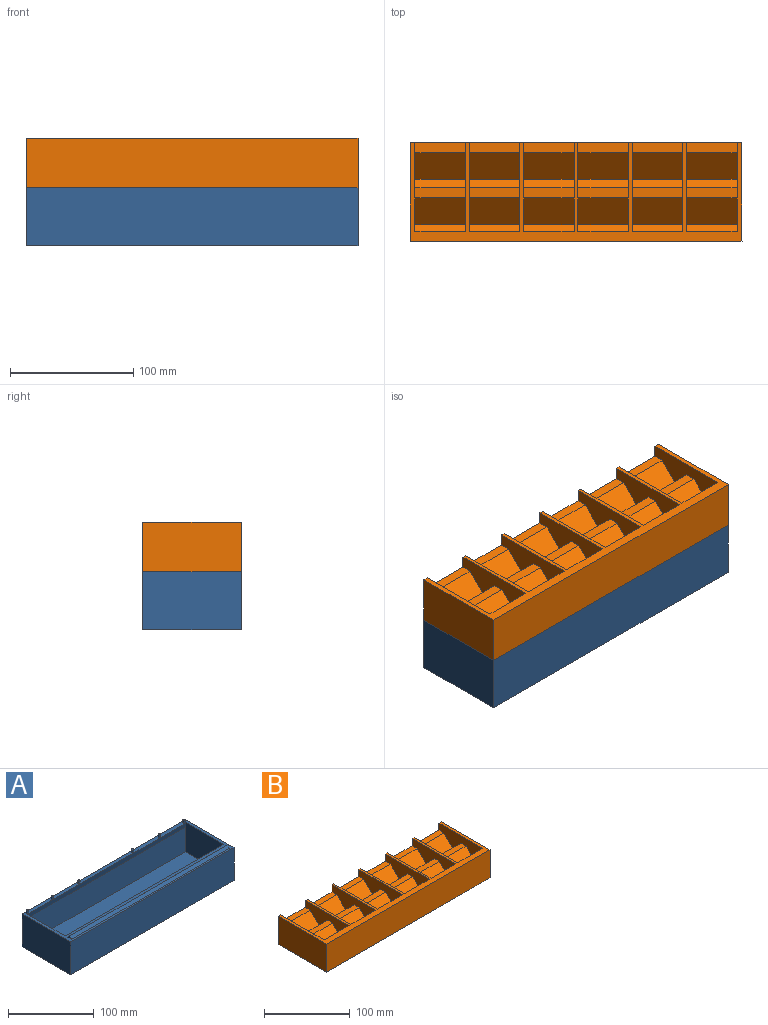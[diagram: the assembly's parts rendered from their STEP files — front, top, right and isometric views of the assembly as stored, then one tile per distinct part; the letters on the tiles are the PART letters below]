
ASSEMBLY  parts=2 mates=1
PART A: 28 faces, bbox 269x80x51 mm
  f0: plane 261x35.19mm, normal (0,-1,0), area 9183.4mm2, adj f1,f2,f4,f15
  f1: plane 63x42mm, normal (1,0,0), area 2641.8mm2, adj f0,f3,f4,f5,f15
  f2: plane 63x42mm, normal (-1,0,0), area 2641.8mm2, adj f0,f3,f4,f5,f15
  f3: plane 261x42mm, normal (0,1,0), area 10962mm2, adj f1,f2,f4,f5
  f4: plane 261x63mm, normal (0,0,1), area 16443mm2, adj f0,f1,f2,f3
  f5: plane 269x80mm, normal (0,0,1), area 3697.2mm2, adj f1,f2,f3,f7,f8,f9,f10,f11
  f6: plane 269x80mm, normal (0,0,-1), area 21520mm2, adj f7,f8,f9,f10
  f7: plane 269x47mm, normal (0,1,0), area 12643mm2, adj f5,f6,f9,f10
  f8: plane 269x47mm, normal (0,-1,0), area 12643mm2, adj f5,f6,f9,f10
  f9: plane 80x47mm, normal (1,0,0), area 3760mm2, adj f5,f6,f7,f8
  f10: plane 80x47mm, normal (-1,0,0), area 3760mm2, adj f5,f6,f7,f8
  f11: plane 260x3.21mm, normal (0,0.71,0.71), area 1179.8mm2, adj f5,f12,f13,f14
  f12: plane 260x3.21mm, normal (0,-0.71,0.71), area 1179.8mm2, adj f5,f11,f13,f14
  f13: plane 6.42x3.21mm, normal (1,0,0), area 10.3mm2, adj f5,f11,f12
  f14: plane 6.42x3.21mm, normal (-1,0,0), area 10.3mm2, adj f5,f11,f12
  f15: plane 261x6.81mm, normal (0,-0.98,-0.18), area 1807.9mm2, adj f0,f1,f2,f5
  f16: cylinder r=1.38mm len=4mm, axis (0,0,-1), area 34.6mm2, adj f5,f17
  f17: plane 2.75x2.75mm, normal (0,0,1), area 5.9mm2, adj f16
  f18: cylinder r=1.38mm len=4mm, axis (0,0,-1), area 34.6mm2, adj f5,f19
  f19: plane 2.75x2.75mm, normal (0,0,1), area 5.9mm2, adj f18
  f20: cylinder r=1.38mm len=4mm, axis (0,0,-1), area 34.6mm2, adj f5,f21
  f21: plane 2.75x2.75mm, normal (0,0,1), area 5.9mm2, adj f20
  f22: cylinder r=1.38mm len=4mm, axis (0,0,-1), area 34.6mm2, adj f5,f23
  f23: plane 2.75x2.75mm, normal (0,0,1), area 5.9mm2, adj f22
  f24: cylinder r=1.38mm len=4mm, axis (0,0,-1), area 34.6mm2, adj f5,f25
  f25: plane 2.75x2.75mm, normal (0,0,1), area 5.9mm2, adj f24
  f26: cylinder r=1.38mm len=4mm, axis (0,0,-1), area 34.6mm2, adj f5,f27
  f27: plane 2.75x2.75mm, normal (0,0,1), area 5.9mm2, adj f26
PART B: 136 faces, bbox 269x80x40 mm
  f0: plane 269x80mm, normal (0,0,-1), area 4885.6mm2, adj f2,f5,f15,f18,f28,f31,f41,f44
  f1: plane 41x12.27mm, normal (0,0.95,-0.31), area 529mm2, adj f12,f13,f88,f114
  f2: plane 41x19.14mm, normal (0,0.71,-0.71), area 1109.6mm2, adj f0,f3,f92,f119
  f3: plane 41x19.14mm, normal (0,-0.71,-0.71), area 1109.6mm2, adj f2,f4,f92,f119
  f4: plane 41x22.37mm, normal (0,0.71,-0.71), area 1296.8mm2, adj f3,f5,f90,f117
  f5: plane 41x22.37mm, normal (0,-1,0), area 917mm2, adj f0,f4,f90,f117
  f6: plane 41x8.1mm, normal (0,0,1), area 332.2mm2, adj f7,f80,f88,f114
  f7: plane 41x21.73mm, normal (0,-0.71,0.71), area 1259.8mm2, adj f6,f8,f88,f114
  f8: plane 41x10.16mm, normal (0,0.71,0.71), area 588.9mm2, adj f7,f9,f88,f114
  f9: plane 41x11.57mm, normal (0,0.96,-0.28), area 494.8mm2, adj f8,f10,f88,f114
  f10: plane 41x8.1mm, normal (0,0,1), area 332.2mm2, adj f9,f11,f88,f114
  f11: plane 41x21.74mm, normal (0,-0.71,0.71), area 1260.8mm2, adj f10,f12,f88,f114
  f12: plane 41x9.47mm, normal (0,0.71,0.71), area 549.2mm2, adj f1,f11,f88,f114
  f13: plane 41x10mm, normal (0,1,0), area 410mm2, adj f1,f83,f88,f114
  f14: plane 41x12.27mm, normal (0,0.95,-0.31), area 529mm2, adj f25,f26,f108,f115
  f15: plane 41x19.14mm, normal (0,0.71,-0.71), area 1109.6mm2, adj f0,f16,f113,f118
  f16: plane 41x19.14mm, normal (0,-0.71,-0.71), area 1109.6mm2, adj f15,f17,f113,f118
  f17: plane 41x22.37mm, normal (0,0.71,-0.71), area 1296.8mm2, adj f16,f18,f111,f116
  f18: plane 41x22.37mm, normal (0,-1,0), area 917mm2, adj f0,f17,f111,f116
  f19: plane 41x8.1mm, normal (0,0,1), area 332.2mm2, adj f20,f80,f108,f115
  f20: plane 41x21.73mm, normal (0,-0.71,0.71), area 1259.8mm2, adj f19,f21,f108,f115
  f21: plane 41x10.16mm, normal (0,0.71,0.71), area 588.9mm2, adj f20,f22,f108,f115
  f22: plane 41x11.57mm, normal (0,0.96,-0.28), area 494.8mm2, adj f21,f23,f108,f115
  f23: plane 41x8.1mm, normal (0,0,1), area 332.2mm2, adj f22,f24,f108,f115
  f24: plane 41x21.74mm, normal (0,-0.71,0.71), area 1260.8mm2, adj f23,f25,f108,f115
  f25: plane 41x9.47mm, normal (0,0.71,0.71), area 549.2mm2, adj f14,f24,f108,f115
  f26: plane 41x10mm, normal (0,1,0), area 410mm2, adj f14,f83,f108,f115
  f27: plane 41x12.27mm, normal (0,0.95,-0.31), area 529mm2, adj f38,f39,f105,f109
  f28: plane 41x19.14mm, normal (0,0.71,-0.71), area 1109.6mm2, adj f0,f29,f107,f112
  f29: plane 41x19.14mm, normal (0,-0.71,-0.71), area 1109.6mm2, adj f28,f30,f107,f112
  f30: plane 41x22.37mm, normal (0,0.71,-0.71), area 1296.8mm2, adj f29,f31,f106,f110
  f31: plane 41x22.37mm, normal (0,-1,0), area 917mm2, adj f0,f30,f106,f110
  f32: plane 41x8.1mm, normal (0,0,1), area 332.2mm2, adj f33,f80,f105,f109
  f33: plane 41x21.73mm, normal (0,-0.71,0.71), area 1259.8mm2, adj f32,f34,f105,f109
  f34: plane 41x10.16mm, normal (0,0.71,0.71), area 588.9mm2, adj f33,f35,f105,f109
  f35: plane 41x11.57mm, normal (0,0.96,-0.28), area 494.8mm2, adj f34,f36,f105,f109
  f36: plane 41x8.1mm, normal (0,0,1), area 332.2mm2, adj f35,f37,f105,f109
  f37: plane 41x21.74mm, normal (0,-0.71,0.71), area 1260.8mm2, adj f36,f38,f105,f109
  f38: plane 41x9.47mm, normal (0,0.71,0.71), area 549.2mm2, adj f27,f37,f105,f109
  f39: plane 41x10mm, normal (0,1,0), area 410mm2, adj f27,f83,f105,f109
  f40: plane 41x12.27mm, normal (0,0.95,-0.31), area 529mm2, adj f51,f52,f84,f99
  f41: plane 41x19.14mm, normal (0,0.71,-0.71), area 1109.6mm2, adj f0,f42,f86,f104
  f42: plane 41x19.14mm, normal (0,-0.71,-0.71), area 1109.6mm2, adj f41,f43,f86,f104
  f43: plane 41x22.37mm, normal (0,0.71,-0.71), area 1296.8mm2, adj f42,f44,f85,f102
  f44: plane 41x22.37mm, normal (0,-1,0), area 917mm2, adj f0,f43,f85,f102
  f45: plane 41x8.1mm, normal (0,0,1), area 332.2mm2, adj f46,f80,f84,f99
  f46: plane 41x21.73mm, normal (0,-0.71,0.71), area 1259.8mm2, adj f45,f47,f84,f99
  f47: plane 41x10.16mm, normal (0,0.71,0.71), area 588.9mm2, adj f46,f48,f84,f99
  f48: plane 41x11.57mm, normal (0,0.96,-0.28), area 494.8mm2, adj f47,f49,f84,f99
  f49: plane 41x8.1mm, normal (0,0,1), area 332.2mm2, adj f48,f50,f84,f99
  f50: plane 41x21.74mm, normal (0,-0.71,0.71), area 1260.8mm2, adj f49,f51,f84,f99
  f51: plane 41x9.47mm, normal (0,0.71,0.71), area 549.2mm2, adj f40,f50,f84,f99
  f52: plane 41x10mm, normal (0,1,0), area 410mm2, adj f40,f83,f84,f99
  f53: plane 41x12.27mm, normal (0,0.95,-0.31), area 529mm2, adj f64,f65,f93,f100
  f54: plane 41x19.14mm, normal (0,0.71,-0.71), area 1109.6mm2, adj f0,f55,f98,f103
  f55: plane 41x19.14mm, normal (0,-0.71,-0.71), area 1109.6mm2, adj f54,f56,f98,f103
  f56: plane 41x22.37mm, normal (0,0.71,-0.71), area 1296.8mm2, adj f55,f57,f96,f101
  f57: plane 41x22.37mm, normal (0,-1,0), area 917mm2, adj f0,f56,f96,f101
  f58: plane 41x8.1mm, normal (0,0,1), area 332.2mm2, adj f59,f80,f93,f100
  f59: plane 41x21.73mm, normal (0,-0.71,0.71), area 1259.8mm2, adj f58,f60,f93,f100
  f60: plane 41x10.16mm, normal (0,0.71,0.71), area 588.9mm2, adj f59,f61,f93,f100
  f61: plane 41x11.57mm, normal (0,0.96,-0.28), area 494.8mm2, adj f60,f62,f93,f100
  f62: plane 41x8.1mm, normal (0,0,1), area 332.2mm2, adj f61,f63,f93,f100
  f63: plane 41x21.74mm, normal (0,-0.71,0.71), area 1260.8mm2, adj f62,f64,f93,f100
  f64: plane 41x9.47mm, normal (0,0.71,0.71), area 549.2mm2, adj f53,f63,f93,f100
  f65: plane 41x10mm, normal (0,1,0), area 410mm2, adj f53,f83,f93,f100
  f66: plane 41x12.27mm, normal (0,0.95,-0.31), area 529mm2, adj f77,f78,f87,f94
  f67: plane 41x19.14mm, normal (0,0.71,-0.71), area 1109.6mm2, adj f0,f68,f91,f97
  f68: plane 41x19.14mm, normal (0,-0.71,-0.71), area 1109.6mm2, adj f67,f69,f91,f97
  f69: plane 41x22.37mm, normal (0,0.71,-0.71), area 1296.8mm2, adj f68,f70,f89,f95
  f70: plane 41x22.37mm, normal (0,-1,0), area 917mm2, adj f0,f69,f89,f95
  f71: plane 41x8.1mm, normal (0,0,1), area 332.2mm2, adj f72,f80,f87,f94
  f72: plane 41x21.73mm, normal (0,-0.71,0.71), area 1259.8mm2, adj f71,f73,f87,f94
  f73: plane 41x10.16mm, normal (0,0.71,0.71), area 588.9mm2, adj f72,f74,f87,f94
  f74: plane 41x11.57mm, normal (0,0.96,-0.28), area 494.8mm2, adj f73,f75,f87,f94
  f75: plane 41x8.1mm, normal (0,0,1), area 332.2mm2, adj f74,f76,f87,f94
  f76: plane 41x21.74mm, normal (0,-0.71,0.71), area 1260.8mm2, adj f75,f77,f87,f94
  f77: plane 41x9.47mm, normal (0,0.71,0.71), area 549.2mm2, adj f66,f76,f87,f94
  f78: plane 41x10mm, normal (0,1,0), area 410mm2, adj f66,f83,f87,f94
  f79: plane 269x40mm, normal (0,-1,0), area 10760mm2, adj f0,f81,f82,f83
  f80: plane 269x40mm, normal (0,1,0), area 8300mm2, adj f0,f6,f19,f32,f45,f58,f71,f81
  f81: plane 80x40mm, normal (1,0,0), area 3200mm2, adj f0,f79,f80,f83
  f82: plane 80x40mm, normal (-1,0,0), area 3200mm2, adj f0,f79,f80,f83
  f83: plane 269x80mm, normal (0,0,1), area 3832.9mm2, adj f13,f26,f39,f52,f65,f78,f79,f80
  f84: plane 75.88x31.74mm, normal (1,0,0), area 1477.4mm2, adj f40,f45,f46,f47,f48,f49,f50,f51
  f85: plane 22.37x22.37mm, normal (1,0,0), area 250.1mm2, adj f0,f43,f44
  f86: plane 38.27x19.14mm, normal (1,0,0), area 366.2mm2, adj f0,f41,f42
  f87: plane 75.88x31.74mm, normal (-1,0,0), area 1477.4mm2, adj f66,f71,f72,f73,f74,f75,f76,f77
  f88: plane 75.88x31.74mm, normal (1,0,0), area 1477.4mm2, adj f1,f6,f7,f8,f9,f10,f11,f12
  f89: plane 22.37x22.37mm, normal (-1,0,0), area 250.1mm2, adj f0,f69,f70
  f90: plane 22.37x22.37mm, normal (1,0,0), area 250.1mm2, adj f0,f4,f5
  f91: plane 38.27x19.14mm, normal (-1,0,0), area 366.2mm2, adj f0,f67,f68
  f92: plane 38.27x19.14mm, normal (1,0,0), area 366.2mm2, adj f0,f2,f3
  f93: plane 75.88x31.74mm, normal (-1,0,0), area 1477.4mm2, adj f53,f58,f59,f60,f61,f62,f63,f64
  f94: plane 75.88x31.74mm, normal (1,0,0), area 1477.4mm2, adj f66,f71,f72,f73,f74,f75,f76,f77
  f95: plane 22.37x22.37mm, normal (1,0,0), area 250.1mm2, adj f0,f69,f70
  f96: plane 22.37x22.37mm, normal (-1,0,0), area 250.1mm2, adj f0,f56,f57
  f97: plane 38.27x19.14mm, normal (1,0,0), area 366.2mm2, adj f0,f67,f68
  f98: plane 38.27x19.14mm, normal (-1,0,0), area 366.2mm2, adj f0,f54,f55
  f99: plane 75.88x31.74mm, normal (-1,0,0), area 1477.4mm2, adj f40,f45,f46,f47,f48,f49,f50,f51
  f100: plane 75.88x31.74mm, normal (1,0,0), area 1477.4mm2, adj f53,f58,f59,f60,f61,f62,f63,f64
  f101: plane 22.37x22.37mm, normal (1,0,0), area 250.1mm2, adj f0,f56,f57
  f102: plane 22.37x22.37mm, normal (-1,0,0), area 250.1mm2, adj f0,f43,f44
  f103: plane 38.27x19.14mm, normal (1,0,0), area 366.2mm2, adj f0,f54,f55
  f104: plane 38.27x19.14mm, normal (-1,0,0), area 366.2mm2, adj f0,f41,f42
  f105: plane 75.88x31.74mm, normal (-1,0,0), area 1477.4mm2, adj f27,f32,f33,f34,f35,f36,f37,f38
  f106: plane 22.37x22.37mm, normal (-1,0,0), area 250.1mm2, adj f0,f30,f31
  f107: plane 38.27x19.14mm, normal (-1,0,0), area 366.2mm2, adj f0,f28,f29
  f108: plane 75.88x31.74mm, normal (-1,0,0), area 1477.4mm2, adj f14,f19,f20,f21,f22,f23,f24,f25
  f109: plane 75.88x31.74mm, normal (1,0,0), area 1477.4mm2, adj f27,f32,f33,f34,f35,f36,f37,f38
  f110: plane 22.37x22.37mm, normal (1,0,0), area 250.1mm2, adj f0,f30,f31
  f111: plane 22.37x22.37mm, normal (-1,0,0), area 250.1mm2, adj f0,f17,f18
  f112: plane 38.27x19.14mm, normal (1,0,0), area 366.2mm2, adj f0,f28,f29
  f113: plane 38.27x19.14mm, normal (-1,0,0), area 366.2mm2, adj f0,f15,f16
  f114: plane 75.88x31.74mm, normal (-1,0,0), area 1477.4mm2, adj f1,f6,f7,f8,f9,f10,f11,f12
  f115: plane 75.88x31.74mm, normal (1,0,0), area 1477.4mm2, adj f14,f19,f20,f21,f22,f23,f24,f25
  f116: plane 22.37x22.37mm, normal (1,0,0), area 250.1mm2, adj f0,f17,f18
  f117: plane 22.37x22.37mm, normal (-1,0,0), area 250.1mm2, adj f0,f4,f5
  f118: plane 38.27x19.14mm, normal (1,0,0), area 366.2mm2, adj f0,f15,f16
  f119: plane 38.27x19.14mm, normal (-1,0,0), area 366.2mm2, adj f0,f2,f3
  f120: plane 261x3.21mm, normal (0,0.71,-0.71), area 1184.3mm2, adj f0,f121,f122,f123
  f121: plane 261x3.21mm, normal (0,-0.71,-0.71), area 1184.3mm2, adj f0,f120,f122,f123
  f122: plane 6.42x3.21mm, normal (-1,0,0), area 10.3mm2, adj f0,f120,f121
  f123: plane 6.42x3.21mm, normal (1,0,0), area 10.3mm2, adj f0,f120,f121
  f124: cylinder r=1.5mm len=3.5mm, axis (0,0,-1), area 33mm2, adj f0,f130
  f125: cylinder r=1.5mm len=3.5mm, axis (0,0,-1), area 33mm2, adj f0,f131
  f126: cylinder r=1.5mm len=3.5mm, axis (0,0,-1), area 33mm2, adj f0,f132
  f127: cylinder r=1.5mm len=3.5mm, axis (0,0,-1), area 33mm2, adj f0,f133
  f128: cylinder r=1.5mm len=3.5mm, axis (0,0,-1), area 33mm2, adj f0,f134
  f129: cylinder r=1.5mm len=3.5mm, axis (0,0,-1), area 33mm2, adj f0,f135
  f130: cone r=1.5mm half-angle=45deg, axis (0,0,-1), area 10mm2, adj f124
  f131: cone r=1.5mm half-angle=45deg, axis (0,0,-1), area 10mm2, adj f125
  f132: cone r=1.5mm half-angle=45deg, axis (0,0,-1), area 10mm2, adj f126
  f133: cone r=1.5mm half-angle=45deg, axis (0,0,-1), area 10mm2, adj f127
  f134: cone r=1.5mm half-angle=45deg, axis (0,0,-1), area 10mm2, adj f128
  f135: cone r=1.5mm half-angle=45deg, axis (0,0,-1), area 10mm2, adj f129
PLACE A t=(-31.85,-16.25,21.13)mm
PLACE B t=(-31.85,81.9,68.13)mm
MATE slider B.f124 <-> A.f26  axis (0,0,-1) through (97.15,78.55,68.13)mm
